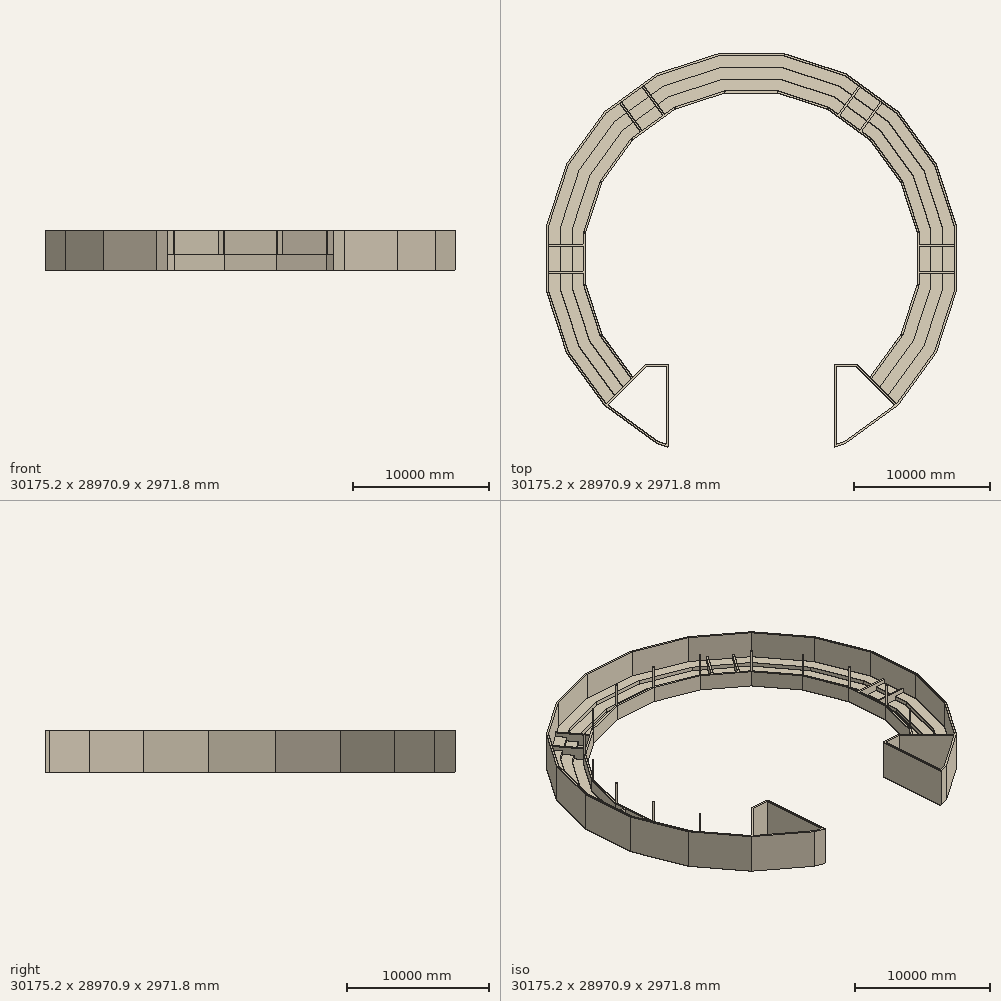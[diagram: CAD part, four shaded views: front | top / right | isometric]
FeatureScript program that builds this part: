
annotation { "Feature Type Name" : "Feature", "Feature Type Description" : "" }
export const myFeature = defineFeature(function(context is Context, id is Id, definition is map)
    precondition{}
    {
        {
            var Q0;
            Q0=qCreatedBy(makeId("Top.planeOp"),FACE);
            var sketch = newSketch(context, id + "F0", { "sketchPlane" : qUnion([Q0])});
            skLineSegment(sketch, "E0.0", {"start": v(-2389.64, 15087.6) * mm, "end": v(2389.64, 15087.6) * mm});
            skLineSegment(sketch, "E0.1", {"start": v(2389.64, 15087.6) * mm, "end": v(6935, 13610.72) * mm});
            skLineSegment(sketch, "E0.2", {"start": v(6935, 13610.72) * mm, "end": v(10801.53, 10801.53) * mm});
            skLineSegment(sketch, "E0.3", {"start": v(10801.53, 10801.53) * mm, "end": v(13610.72, 6935) * mm});
            skLineSegment(sketch, "E0.4", {"start": v(13610.72, 6935) * mm, "end": v(15087.6, 2389.64) * mm});
            skLineSegment(sketch, "E0.5", {"start": v(15087.6, 2389.64) * mm, "end": v(15087.6, -2389.64) * mm});
            skLineSegment(sketch, "E0.6", {"start": v(15087.6, -2389.64) * mm, "end": v(13610.72, -6935) * mm});
            skLineSegment(sketch, "E0.7", {"start": v(13610.72, -6935) * mm, "end": v(10801.53, -10801.53) * mm});
            skLineSegment(sketch, "E0.8", {"start": v(10801.53, -10801.53) * mm, "end": v(6935, -13610.72) * mm});
            skLineSegment(sketch, "E0.9", {"start": v(6935, -13610.72) * mm, "end": v(6096, -13883.33) * mm});
            skLineSegment(sketch, "E0.11", {"start": v(-6096, -13883.33) * mm, "end": v(-6935, -13610.72) * mm});
            skLineSegment(sketch, "E0.12", {"start": v(-6935, -13610.72) * mm, "end": v(-10801.53, -10801.53) * mm});
            skLineSegment(sketch, "E0.13", {"start": v(-10801.53, -10801.53) * mm, "end": v(-13610.72, -6935) * mm});
            skLineSegment(sketch, "E0.14", {"start": v(-13610.72, -6935) * mm, "end": v(-15087.6, -2389.64) * mm});
            skLineSegment(sketch, "E0.15", {"start": v(-15087.6, -2389.64) * mm, "end": v(-15087.6, 2389.64) * mm});
            skLineSegment(sketch, "E0.16", {"start": v(-15087.6, 2389.64) * mm, "end": v(-13610.72, 6935) * mm});
            skLineSegment(sketch, "E0.17", {"start": v(-13610.72, 6935) * mm, "end": v(-10801.53, 10801.53) * mm});
            skLineSegment(sketch, "E0.18", {"start": v(-10801.53, 10801.53) * mm, "end": v(-6935, 13610.72) * mm});
            skLineSegment(sketch, "E0.19", {"start": v(-6935, 13610.72) * mm, "end": v(-2389.64, 15087.6) * mm});
            skLineSegment(sketch, "E1", {"start": v(-6096, -7772.4) * mm, "end": v(-6096, -13883.33) * mm});
            skLineSegment(sketch, "E2", {"start": v(6096, -7772.4) * mm, "end": v(6096, -13883.33) * mm});
            skLineSegment(sketch, "E3", {"start": v(-7772.4, -7772.4) * mm, "end": v(-6096, -7772.4) * mm});
            skLineSegment(sketch, "E4", {"start": v(6096, -7772.4) * mm, "end": v(6705.6, -7772.4) * mm});
            skLineSegment(sketch, "E5.0", {"start": v(-1931.02, 12192) * mm, "end": v(1931.02, 12192) * mm});
            skLineSegment(sketch, "E5.1", {"start": v(1931.02, 12192) * mm, "end": v(5604.05, 10998.56) * mm});
            skLineSegment(sketch, "E5.2", {"start": v(5604.05, 10998.56) * mm, "end": v(6426.51, 10401) * mm});
            skLineSegment(sketch, "E5.3", {"start": v(8728.5, 8728.5) * mm, "end": v(10998.56, 5604.05) * mm});
            skLineSegment(sketch, "E5.4", {"start": v(10998.56, 5604.05) * mm, "end": v(12192, 1931.02) * mm});
            skLineSegment(sketch, "E5.5", {"start": v(12192, 1931.02) * mm, "end": v(12192, 914.4) * mm});
            skLineSegment(sketch, "E5.6", {"start": v(12192, -1931.02) * mm, "end": v(10998.56, -5604.05) * mm});
            skLineSegment(sketch, "E5.13", {"start": v(-8728.5, -8728.5) * mm, "end": v(-10998.56, -5604.05) * mm});
            skLineSegment(sketch, "E5.14", {"start": v(-10998.56, -5604.05) * mm, "end": v(-12192, -1931.02) * mm});
            skLineSegment(sketch, "E5.15", {"start": v(-12192, -1931.02) * mm, "end": v(-12192, -914.4) * mm});
            skLineSegment(sketch, "E5.16", {"start": v(-12192, 1931.02) * mm, "end": v(-10998.56, 5604.05) * mm});
            skLineSegment(sketch, "E5.17", {"start": v(-10998.56, 5604.05) * mm, "end": v(-8728.5, 8728.5) * mm});
            skLineSegment(sketch, "E5.18", {"start": v(-8728.5, 8728.5) * mm, "end": v(-7953.14, 9291.85) * mm});
            skLineSegment(sketch, "E5.19", {"start": v(-5604.05, 10998.56) * mm, "end": v(-1931.02, 12192) * mm});
            skLineSegment(sketch, "E6", {"start": v(-15087.6, 0) * mm, "end": v(-15087.6, 914.4) * mm});
            skLineSegment(sketch, "E7", {"start": v(-14935.2, 914.4) * mm, "end": v(-12344.4, 914.4) * mm});
            skPoint(sketch, "E7.endSnap0", {"position": v(15087.6, 0) * mm});
            skLineSegment(sketch, "E8", {"start": v(15087.6, 914.4) * mm, "end": v(15087.6, -914.4) * mm});
            skLineSegment(sketch, "E9", {"start": v(14935.2, -914.4) * mm, "end": v(12344.4, -914.4) * mm});
            skLineSegment(sketch, "E10.trimOffspring", {"start": v(12344.4, 914.4) * mm, "end": v(14935.2, 914.4) * mm});
            skLineSegment(sketch, "E11.trimOffspring", {"start": v(-12344.4, -914.4) * mm, "end": v(-14935.2, -914.4) * mm});
            skLineSegment(sketch, "E12.trimOffspring", {"start": v(-12192, 914.4) * mm, "end": v(-12192, 1931.02) * mm});
            skLineSegment(sketch, "E13.trimOffspring", {"start": v(12192, -914.4) * mm, "end": v(12192, -1931.02) * mm});
            skLineSegment(sketch, "E14", {"start": v(-8042.71, 9415.14) * mm, "end": v(-9565.55, 11511.14) * mm});
            skLineSegment(sketch, "E15", {"start": v(-9655.13, 11634.44) * mm, "end": v(-8128.5, 12743.6) * mm});
            skLineSegment(sketch, "E16", {"start": v(-8038.93, 12620.3) * mm, "end": v(-6516.1, 10524.3) * mm});
            skLineSegment(sketch, "E17.trimOffspring", {"start": v(-6426.51, 10401) * mm, "end": v(-5604.05, 10998.56) * mm});
            skLineSegment(sketch, "E18.MirrorCS", {"start": v(8038.93, 12620.3) * mm, "end": v(6516.1, 10524.3) * mm});
            skLineSegment(sketch, "E19.MirrorCS", {"start": v(7995.62, 9449.36) * mm, "end": v(9518.46, 11545.36) * mm});
            skLineSegment(sketch, "E20.trimOffspring", {"start": v(7906.04, 9326.06) * mm, "end": v(8728.5, 8728.5) * mm});
            skLineSegment(sketch, "E21.0", {"start": v(-2365.5, 14935.2) * mm, "end": v(2365.5, 14935.2) * mm});
            skLineSegment(sketch, "E21.1", {"start": v(2365.5, 14935.2) * mm, "end": v(6864.96, 13473.24) * mm});
            skLineSegment(sketch, "E21.2", {"start": v(6864.96, 13473.24) * mm, "end": v(7915.63, 12709.88) * mm});
            skLineSegment(sketch, "E21.3", {"start": v(10692.42, 10692.42) * mm, "end": v(13473.24, 6864.96) * mm});
            skLineSegment(sketch, "E21.4", {"start": v(13473.24, 6864.96) * mm, "end": v(14935.2, 2365.5) * mm});
            skLineSegment(sketch, "E21.5", {"start": v(14935.2, 2365.5) * mm, "end": v(14935.2, 1066.8) * mm});
            skLineSegment(sketch, "E21.6", {"start": v(14935.2, -2365.5) * mm, "end": v(13473.24, -6864.96) * mm});
            skLineSegment(sketch, "E21.12", {"start": v(-6864.96, -13473.24) * mm, "end": v(-10692.42, -10692.42) * mm});
            skLineSegment(sketch, "E21.13", {"start": v(-10692.42, -10692.42) * mm, "end": v(-13473.24, -6864.96) * mm});
            skLineSegment(sketch, "E21.14", {"start": v(-13473.24, -6864.96) * mm, "end": v(-14935.2, -2365.5) * mm});
            skLineSegment(sketch, "E21.15", {"start": v(-14935.2, -2365.5) * mm, "end": v(-14935.2, -1066.8) * mm});
            skLineSegment(sketch, "E21.16", {"start": v(-14935.2, 2365.5) * mm, "end": v(-13473.24, 6864.96) * mm});
            skLineSegment(sketch, "E21.17", {"start": v(-13473.24, 6864.96) * mm, "end": v(-10692.42, 10692.42) * mm});
            skLineSegment(sketch, "E21.18", {"start": v(-10692.42, 10692.42) * mm, "end": v(-9688.84, 11421.57) * mm});
            skLineSegment(sketch, "E21.19", {"start": v(-6864.96, 13473.24) * mm, "end": v(-2365.5, 14935.2) * mm});
            skLineSegment(sketch, "E22.trimOffspring", {"start": v(-7915.63, 12709.88) * mm, "end": v(-6864.96, 13473.24) * mm});
            skLineSegment(sketch, "E23", {"start": v(0, 12192) * mm, "end": v(0, 12344.4) * mm});
            skLineSegment(sketch, "E24.0", {"start": v(-1955.16, 12344.4) * mm, "end": v(1955.16, 12344.4) * mm});
            skLineSegment(sketch, "E24.1", {"start": v(1955.16, 12344.4) * mm, "end": v(5674.1, 11136.04) * mm});
            skLineSegment(sketch, "E24.2", {"start": v(5674.1, 11136.04) * mm, "end": v(6392.8, 10613.88) * mm});
            skLineSegment(sketch, "E24.3", {"start": v(8837.61, 8837.61) * mm, "end": v(11136.04, 5674.1) * mm});
            skLineSegment(sketch, "E24.4", {"start": v(11136.04, 5674.1) * mm, "end": v(12344.4, 1955.16) * mm});
            skLineSegment(sketch, "E24.5", {"start": v(12344.4, 1955.16) * mm, "end": v(12344.4, 1066.8) * mm});
            skLineSegment(sketch, "E24.6", {"start": v(12344.4, -1955.16) * mm, "end": v(11136.04, -5674.1) * mm});
            skLineSegment(sketch, "E24.13", {"start": v(-8837.61, -8837.61) * mm, "end": v(-11136.04, -5674.1) * mm});
            skLineSegment(sketch, "E24.14", {"start": v(-11136.04, -5674.1) * mm, "end": v(-12344.4, -1955.16) * mm});
            skLineSegment(sketch, "E24.15", {"start": v(-12344.4, -1955.16) * mm, "end": v(-12344.4, -1066.8) * mm});
            skLineSegment(sketch, "E24.16", {"start": v(-12344.4, 1955.16) * mm, "end": v(-11136.04, 5674.1) * mm});
            skLineSegment(sketch, "E24.17", {"start": v(-11136.04, 5674.1) * mm, "end": v(-8837.61, 8837.61) * mm});
            skLineSegment(sketch, "E24.18", {"start": v(-8837.61, 8837.61) * mm, "end": v(-8166, 9325.56) * mm});
            skLineSegment(sketch, "E24.19", {"start": v(-5674.1, 11136.04) * mm, "end": v(-1955.16, 12344.4) * mm});
            skPoint(sketch, "E24.0.midPoint", {"position": v(0, 12344.4) * mm});
            skLineSegment(sketch, "E25.trimOffspring", {"start": v(-6392.8, 10613.88) * mm, "end": v(-5674.1, 11136.04) * mm});
            skLineSegment(sketch, "E26.trimOffspring", {"start": v(8118.92, 9359.78) * mm, "end": v(8837.61, 8837.61) * mm});
            skLineSegment(sketch, "E27", {"start": v(-10692.42, -10692.42) * mm, "end": v(-7772.4, -7772.4) * mm});
            skLineSegment(sketch, "E28", {"start": v(-8837.61, -8837.61) * mm, "end": v(-10692.42, -10692.42) * mm});
            skLineSegment(sketch, "E29", {"start": v(-7709.27, -7924.8) * mm, "end": v(-10567.6, -10783.12) * mm});
            skLineSegment(sketch, "E30", {"start": v(-6096, -7772.4) * mm, "end": v(-6096, -7924.8) * mm});
            skLineSegment(sketch, "E31", {"start": v(-6248.4, -7924.8) * mm, "end": v(-7709.27, -7924.8) * mm});
            skPoint(sketch, "E32.orphan", {"position": v(-7556.87, -7772.4) * mm});
            skLineSegment(sketch, "E33", {"start": v(-6248.4, -7924.8) * mm, "end": v(-6248.4, -13673.57) * mm});
            skLineSegment(sketch, "E34.trimOffspring", {"start": v(-6248.4, -13673.57) * mm, "end": v(-6864.96, -13473.24) * mm});
            skLineSegment(sketch, "E35.MirrorCS", {"start": v(8728.5, -8728.5) * mm, "end": v(10998.56, -5604.05) * mm});
            skLineSegment(sketch, "E36.MirrorCS", {"start": v(7709.27, -7924.8) * mm, "end": v(10567.6, -10783.12) * mm});
            skLineSegment(sketch, "E37.MirrorCS", {"start": v(6248.4, -7924.8) * mm, "end": v(7709.27, -7924.8) * mm});
            skLineSegment(sketch, "E38.MirrorCS", {"start": v(7772.4, -7772.4) * mm, "end": v(6096, -7772.4) * mm});
            skPoint(sketch, "E39.MirrorP", {"position": v(7556.87, -7772.4) * mm});
            skLineSegment(sketch, "E40.MirrorCS", {"start": v(8837.61, -8837.61) * mm, "end": v(11136.04, -5674.1) * mm});
            skLineSegment(sketch, "E41.MirrorCS", {"start": v(10692.42, -10692.42) * mm, "end": v(7772.4, -7772.4) * mm});
            skLineSegment(sketch, "E42.MirrorCS", {"start": v(8837.61, -8837.61) * mm, "end": v(10692.42, -10692.42) * mm});
            skLineSegment(sketch, "E43.MirrorCS", {"start": v(6864.96, -13473.24) * mm, "end": v(10692.42, -10692.42) * mm});
            skLineSegment(sketch, "E44.MirrorCS", {"start": v(10692.42, -10692.42) * mm, "end": v(13473.24, -6864.96) * mm});
            skLineSegment(sketch, "E45.MirrorCS", {"start": v(6248.4, -13673.57) * mm, "end": v(6864.96, -13473.24) * mm});
            skLineSegment(sketch, "E46.MirrorCS", {"start": v(6248.4, -7924.8) * mm, "end": v(6248.4, -13673.57) * mm});
            skLineSegment(sketch, "E47.trimOffspring", {"start": v(-12344.4, 1066.8) * mm, "end": v(-12344.4, 1955.16) * mm});
            skLineSegment(sketch, "E48.trimOffspring", {"start": v(-14935.2, 1066.8) * mm, "end": v(-14935.2, 2365.5) * mm});
            skLineSegment(sketch, "E49", {"start": v(-14935.2, -1066.8) * mm, "end": v(-12344.4, -1066.8) * mm});
            skLineSegment(sketch, "E50.0", {"start": v(-14071.6, -2228.72) * mm, "end": v(-14071.6, -1066.8) * mm});
            skLineSegment(sketch, "E50.1", {"start": v(-14071.6, 2228.72) * mm, "end": v(-12694.17, 6468) * mm});
            skLineSegment(sketch, "E50.2", {"start": v(-12694.17, 6468) * mm, "end": v(-10074.15, 10074.15) * mm});
            skLineSegment(sketch, "E50.3", {"start": v(-10074.15, 10074.15) * mm, "end": v(-9181.23, 10722.9) * mm});
            skLineSegment(sketch, "E50.4", {"start": v(-6468, 12694.17) * mm, "end": v(-2228.72, 14071.6) * mm});
            skLineSegment(sketch, "E50.5", {"start": v(-2228.72, 14071.6) * mm, "end": v(2228.72, 14071.6) * mm});
            skLineSegment(sketch, "E50.6", {"start": v(2228.72, 14071.6) * mm, "end": v(6468, 12694.17) * mm});
            skLineSegment(sketch, "E50.7", {"start": v(6468, 12694.17) * mm, "end": v(7408.02, 12011.21) * mm});
            skLineSegment(sketch, "E50.8", {"start": v(10074.15, 10074.15) * mm, "end": v(12694.17, 6468) * mm});
            skLineSegment(sketch, "E50.9", {"start": v(12694.17, 6468) * mm, "end": v(14071.6, 2228.72) * mm});
            skLineSegment(sketch, "E50.10", {"start": v(14071.6, 2228.72) * mm, "end": v(14071.6, 1066.8) * mm});
            skLineSegment(sketch, "E50.11", {"start": v(14071.6, -2228.72) * mm, "end": v(12694.17, -6468) * mm});
            skLineSegment(sketch, "E50.12", {"start": v(12694.17, -6468) * mm, "end": v(10074.15, -10074.15) * mm});
            skLineSegment(sketch, "E50.18", {"start": v(-10074.15, -10074.15) * mm, "end": v(-12694.17, -6468) * mm});
            skLineSegment(sketch, "E50.19", {"start": v(-12694.17, -6468) * mm, "end": v(-14071.6, -2228.72) * mm});
            skLineSegment(sketch, "E51.0", {"start": v(-13208, -2091.94) * mm, "end": v(-13208, -1066.8) * mm});
            skLineSegment(sketch, "E51.1", {"start": v(-13208, 2091.94) * mm, "end": v(-11915.1, 6071.05) * mm});
            skLineSegment(sketch, "E51.2", {"start": v(-11915.1, 6071.05) * mm, "end": v(-9455.88, 9455.88) * mm});
            skLineSegment(sketch, "E51.3", {"start": v(-9455.88, 9455.88) * mm, "end": v(-8673.62, 10024.23) * mm});
            skLineSegment(sketch, "E51.4", {"start": v(-6071.05, 11915.1) * mm, "end": v(-2091.94, 13208) * mm});
            skLineSegment(sketch, "E51.5", {"start": v(-2091.94, 13208) * mm, "end": v(2091.94, 13208) * mm});
            skLineSegment(sketch, "E51.6", {"start": v(2091.94, 13208) * mm, "end": v(6071.05, 11915.1) * mm});
            skLineSegment(sketch, "E51.8", {"start": v(9455.88, 9455.88) * mm, "end": v(11915.1, 6071.05) * mm});
            skLineSegment(sketch, "E51.9", {"start": v(11915.1, 6071.05) * mm, "end": v(13208, 2091.94) * mm});
            skLineSegment(sketch, "E51.10", {"start": v(13208, 2091.94) * mm, "end": v(13208, 1066.8) * mm});
            skLineSegment(sketch, "E51.11", {"start": v(13208, -2091.94) * mm, "end": v(11915.1, -6071.05) * mm});
            skLineSegment(sketch, "E51.12", {"start": v(11915.1, -6071.05) * mm, "end": v(9455.88, -9455.88) * mm});
            skLineSegment(sketch, "E51.18", {"start": v(-9455.88, -9455.88) * mm, "end": v(-11915.1, -6071.05) * mm});
            skLineSegment(sketch, "E51.19", {"start": v(-11915.1, -6071.05) * mm, "end": v(-13208, -2091.94) * mm});
            skLineSegment(sketch, "E52.trimOffspring", {"start": v(-14071.6, 1066.8) * mm, "end": v(-14071.6, 2228.72) * mm});
            skLineSegment(sketch, "E53", {"start": v(-13208, 2091.94) * mm, "end": v(-13208, 1066.8) * mm});
            skLineSegment(sketch, "E54", {"start": v(-14935.2, 1066.8) * mm, "end": v(-12344.4, 1066.8) * mm});
            skLineSegment(sketch, "E55", {"start": v(-9688.84, 11421.57) * mm, "end": v(-8166, 9325.56) * mm});
            skLineSegment(sketch, "E56", {"start": v(-7915.63, 12709.88) * mm, "end": v(-6392.8, 10613.88) * mm});
            skLineSegment(sketch, "E57.trimOffspring", {"start": v(-7408.02, 12011.21) * mm, "end": v(-6468, 12694.17) * mm});
            skLineSegment(sketch, "E58.trimOffspring", {"start": v(-6900.4, 11312.55) * mm, "end": v(-6071.05, 11915.1) * mm});
            skLineSegment(sketch, "E59", {"start": v(6392.8, 10613.88) * mm, "end": v(7915.63, 12709.88) * mm});
            skLineSegment(sketch, "E60.trimOffspring", {"start": v(9134.14, 10757.11) * mm, "end": v(10074.15, 10074.15) * mm});
            skLineSegment(sketch, "E61.trimOffspring", {"start": v(8626.53, 10058.45) * mm, "end": v(9455.88, 9455.88) * mm});
            skLineSegment(sketch, "E62.trimOffspring", {"start": v(9641.75, 11455.78) * mm, "end": v(10692.42, 10692.42) * mm});
            skLineSegment(sketch, "E63", {"start": v(8118.92, 9359.78) * mm, "end": v(9641.75, 11455.78) * mm});
            skLineSegment(sketch, "E64", {"start": v(6071.05, 11915.1) * mm, "end": v(6900.4, 11312.55) * mm});
            skLineSegment(sketch, "E65.trimOffspring", {"start": v(12344.4, -1066.8) * mm, "end": v(12344.4, -1955.16) * mm});
            skLineSegment(sketch, "E66.trimOffspring", {"start": v(13208, -1066.8) * mm, "end": v(13208, -2091.94) * mm});
            skLineSegment(sketch, "E67.trimOffspring", {"start": v(14071.6, -1066.8) * mm, "end": v(14071.6, -2228.72) * mm});
            skLineSegment(sketch, "E68", {"start": v(12344.4, 1066.8) * mm, "end": v(14935.2, 1066.8) * mm});
            skLineSegment(sketch, "E69", {"start": v(12344.4, -1066.8) * mm, "end": v(14935.2, -1066.8) * mm});
            skLineSegment(sketch, "E70.trimOffspring", {"start": v(14935.2, -1066.8) * mm, "end": v(14935.2, -2365.5) * mm});
            skLineSegment(sketch, "E71", {"start": v(-8038.93, 12620.3) * mm, "end": v(-9565.55, 11511.14) * mm});
            skLineSegment(sketch, "E72", {"start": v(8038.93, 12620.3) * mm, "end": v(9518.46, 11545.36) * mm});
            skLineSegment(sketch, "E73", {"start": v(14935.2, -914.4) * mm, "end": v(14935.2, 914.4) * mm});
            skLineSegment(sketch, "E74", {"start": v(-14935.2, 914.4) * mm, "end": v(-14935.2, -914.4) * mm});
            skLineSegment(sketch, "E75", {"start": v(-14935.2, -914.4) * mm, "end": v(-14935.2, -1066.8) * mm});
            skLineSegment(sketch, "E76", {"start": v(-14935.2, 1066.8) * mm, "end": v(-14935.2, 914.4) * mm});
            skLineSegment(sketch, "E77", {"start": v(-9565.55, 11511.14) * mm, "end": v(-9688.84, 11421.57) * mm});
            skLineSegment(sketch, "E78", {"start": v(-7915.63, 12709.88) * mm, "end": v(-8038.93, 12620.3) * mm});
            skLineSegment(sketch, "E79", {"start": v(7915.63, 12709.88) * mm, "end": v(8038.93, 12620.3) * mm});
            skLineSegment(sketch, "E80", {"start": v(9518.46, 11545.36) * mm, "end": v(9641.75, 11455.78) * mm});
            skLineSegment(sketch, "E81", {"start": v(14935.2, 1066.8) * mm, "end": v(14935.2, 914.4) * mm});
            skLineSegment(sketch, "E82", {"start": v(14935.2, -914.4) * mm, "end": v(14935.2, -1066.8) * mm});
            skCircle(sketch, "E83", {"center": v(-11067.3, -5639.07) * mm, "radius": 60.96 * mm});
            skCircle(sketch, "E84.7.0", {"center": v(11067.3, -5639.07) * mm, "radius": 60.96 * mm});
            skCircle(sketch, "E84.8.0", {"center": v(12268.2, -1943.1) * mm, "radius": 60.96 * mm});
            skCircle(sketch, "E84.9.0", {"center": v(12268.2, 1943.1) * mm, "radius": 60.96 * mm});
            skCircle(sketch, "E84.10.0", {"center": v(11067.3, 5639.07) * mm, "radius": 60.96 * mm});
            skCircle(sketch, "E84.11.0", {"center": v(8783.06, 8783.06) * mm, "radius": 60.96 * mm});
            skCircle(sketch, "E84.12.0", {"center": v(5639.07, 11067.3) * mm, "radius": 60.96 * mm});
            skCircle(sketch, "E84.13.0", {"center": v(1943.1, 12268.2) * mm, "radius": 60.96 * mm});
            skCircle(sketch, "E84.14.0", {"center": v(-1943.1, 12268.2) * mm, "radius": 60.96 * mm});
            skCircle(sketch, "E84.15.0", {"center": v(-5639.07, 11067.3) * mm, "radius": 60.96 * mm});
            skCircle(sketch, "E84.16.0", {"center": v(-8783.06, 8783.06) * mm, "radius": 60.96 * mm});
            skCircle(sketch, "E84.17.0", {"center": v(-11067.3, 5639.07) * mm, "radius": 60.96 * mm});
            skCircle(sketch, "E84.18.0", {"center": v(-12268.2, 1943.1) * mm, "radius": 60.96 * mm});
            skCircle(sketch, "E84.19.0", {"center": v(-12268.2, -1943.1) * mm, "radius": 60.96 * mm});
            skLineSegment(sketch, "E85", {"start": v(-9057.94, 10812.48) * mm, "end": v(-7531.31, 11921.63) * mm});
            skLineSegment(sketch, "E86", {"start": v(-8550.33, 10113.81) * mm, "end": v(-7023.7, 11222.97) * mm});
            skLineSegment(sketch, "E87", {"start": v(-7953.14, 9291.85) * mm, "end": v(-6426.51, 10401) * mm});
            skLineSegment(sketch, "E88", {"start": v(-6516.1, 10524.3) * mm, "end": v(-8042.71, 9415.14) * mm});
            skLineSegment(sketch, "E89", {"start": v(-14071.6, 914.4) * mm, "end": v(-14071.6, -914.4) * mm});
            skLineSegment(sketch, "E90", {"start": v(-13208, 914.4) * mm, "end": v(-13208, -914.4) * mm});
            skLineSegment(sketch, "E91", {"start": v(-12344.4, 914.4) * mm, "end": v(-12344.4, -914.4) * mm});
            skLineSegment(sketch, "E92", {"start": v(-12192, 914.4) * mm, "end": v(-12192, -914.4) * mm});
            skLineSegment(sketch, "E93", {"start": v(6426.51, 10401) * mm, "end": v(7906.04, 9326.06) * mm});
            skLineSegment(sketch, "E94", {"start": v(6516.1, 10524.3) * mm, "end": v(7995.62, 9449.36) * mm});
            skLineSegment(sketch, "E95", {"start": v(7023.7, 11222.97) * mm, "end": v(8503.23, 10148.03) * mm});
            skLineSegment(sketch, "E96", {"start": v(7531.31, 11921.63) * mm, "end": v(9010.84, 10846.7) * mm});
            skLineSegment(sketch, "E97", {"start": v(12192, 914.4) * mm, "end": v(12192, -914.4) * mm});
            skLineSegment(sketch, "E98", {"start": v(12344.4, 914.4) * mm, "end": v(12344.4, -914.4) * mm});
            skLineSegment(sketch, "E99", {"start": v(14071.6, 914.4) * mm, "end": v(14071.6, -914.4) * mm});
            skLineSegment(sketch, "E100", {"start": v(13208, 914.4) * mm, "end": v(13208, -914.4) * mm});
            skSolve(sketch);
        }
        {
            var Q0;
            Q0=makeQuery(id+"F0.imprint","IMPRINT",FACE,{"disambiguationData":[TD([[makeQuery(id+"F0.imprint","IMPRINT",EDGE,{"derivedFrom":sQuery(id+"F0.wireOp",EDGE,"E0.0")}),-1.0]])]});
            extrude(context, id + "F1", {"entities" : qUnion([Q0]), "depth" : 2971.8 * mm, "offsetDistance" : 30.48 * mm});
        }
        {
            var Q0;
            {var subQ2=sQuery(id+"F0.wireOp",EDGE,"E24.13");Q0=makeQuery(id+"F0.imprint","IMPRINT",FACE,{"disambiguationData":[TD([[makeQuery(id+"F0.imprint","IMPRINT",EDGE,{"derivedFrom":subQ2}),1.0]])]});}
            var Q1;
            Q1=makeQuery(id+"F0.imprint","IMPRINT",FACE,{"disambiguationData":[TD([[makeQuery(id+"F0.imprint","IMPRINT",EDGE,{"derivedFrom":sQuery(id+"F0.wireOp",EDGE,"E24.16")}),1.0]])]});
            var Q2;
            Q2=makeQuery(id+"F0.imprint","IMPRINT",FACE,{"disambiguationData":[TD([[makeQuery(id+"F0.imprint","IMPRINT",EDGE,{"derivedFrom":sQuery(id+"F0.wireOp",EDGE,"E24.6")}),1.0]])]});
            var Q3;
            Q3=makeQuery(id+"F0.imprint","IMPRINT",FACE,{"disambiguationData":[TD([[makeQuery(id+"F0.imprint","IMPRINT",EDGE,{"derivedFrom":sQuery(id+"F0.wireOp",EDGE,"E24.3")}),1.0]])]});
            var Q4;
            {var subQ9=sQuery(id+"F0.wireOp",EDGE,"E24.1");Q4=makeQuery(id+"F0.imprint","IMPRINT",FACE,{"disambiguationData":[TD([[makeQuery(id+"F0.imprint","IMPRINT",EDGE,{"derivedFrom":subQ9}),1.0]])]});}
            var Q5;
            {var subQ2=sQuery(id+"F0.wireOp",EDGE,"E90");Q5=makeQuery(id+"F0.imprint","IMPRINT",FACE,{"disambiguationData":[TD([[makeQuery(id+"F0.imprint","IMPRINT",EDGE,{"derivedFrom":subQ2}),1.0]])]});}
            var Q6;
            {var subQ2=sQuery(id+"F0.wireOp",EDGE,"E86");Q6=makeQuery(id+"F0.imprint","IMPRINT",FACE,{"disambiguationData":[TD([[makeQuery(id+"F0.imprint","IMPRINT",EDGE,{"derivedFrom":subQ2}),-1.0]])]});}
            var Q7;
            {var subQ0=sQuery(id+"F0.wireOp",EDGE,"E94");Q7=makeQuery(id+"F0.imprint","IMPRINT",FACE,{"disambiguationData":[TD([[makeQuery(id+"F0.imprint","IMPRINT",EDGE,{"derivedFrom":subQ0}),1.0]])]});}
            var Q8;
            {var subQ0=sQuery(id+"F0.wireOp",EDGE,"E98");Q8=makeQuery(id+"F0.imprint","IMPRINT",FACE,{"disambiguationData":[TD([[makeQuery(id+"F0.imprint","IMPRINT",EDGE,{"derivedFrom":subQ0}),1.0]])]});}
            extrude(context, id + "F2", {"entities" : qUnion([Q0, Q1, Q2, Q3, Q4, Q5, Q6, Q7, Q8]), "depth" : 304.8 * mm, "offsetDistance" : 30.48 * mm});
        }
        {
            var Q0;
            Q0=makeQuery(id+"F0.imprint","IMPRINT",FACE,{"disambiguationData":[TD([[makeQuery(id+"F0.imprint","IMPRINT",EDGE,{"derivedFrom":sQuery(id+"F0.wireOp",EDGE,"E50.1")}),-1.0]])]});
            var Q1;
            {var subQ0=sQuery(id+"F0.wireOp",EDGE,"E50.0");Q1=makeQuery(id+"F0.imprint","IMPRINT",FACE,{"disambiguationData":[TD([[makeQuery(id+"F0.imprint","IMPRINT",EDGE,{"derivedFrom":subQ0}),-1.0]])]});}
            var Q2;
            Q2=makeQuery(id+"F0.imprint","IMPRINT",FACE,{"disambiguationData":[TD([[makeQuery(id+"F0.imprint","IMPRINT",EDGE,{"derivedFrom":sQuery(id+"F0.wireOp",EDGE,"E50.4")}),-1.0]])]});
            var Q3;
            Q3=makeQuery(id+"F0.imprint","IMPRINT",FACE,{"disambiguationData":[TD([[makeQuery(id+"F0.imprint","IMPRINT",EDGE,{"derivedFrom":sQuery(id+"F0.wireOp",EDGE,"E50.8")}),-1.0]])]});
            var Q4;
            Q4=makeQuery(id+"F0.imprint","IMPRINT",FACE,{"disambiguationData":[TD([[makeQuery(id+"F0.imprint","IMPRINT",EDGE,{"derivedFrom":sQuery(id+"F0.wireOp",EDGE,"E50.11")}),-1.0]])]});
            var Q5;
            {var subQ0=sQuery(id+"F0.wireOp",EDGE,"E89");Q5=makeQuery(id+"F0.imprint","IMPRINT",FACE,{"disambiguationData":[TD([[makeQuery(id+"F0.imprint","IMPRINT",EDGE,{"derivedFrom":subQ0}),1.0]])]});}
            var Q6;
            {var subQ0=sQuery(id+"F0.wireOp",EDGE,"E85");Q6=makeQuery(id+"F0.imprint","IMPRINT",FACE,{"disambiguationData":[TD([[makeQuery(id+"F0.imprint","IMPRINT",EDGE,{"derivedFrom":subQ0}),-1.0]])]});}
            var Q7;
            {var subQ0=sQuery(id+"F0.wireOp",EDGE,"E95");Q7=makeQuery(id+"F0.imprint","IMPRINT",FACE,{"disambiguationData":[TD([[makeQuery(id+"F0.imprint","IMPRINT",EDGE,{"derivedFrom":subQ0}),1.0]])]});}
            var Q8;
            {var subQ0=sQuery(id+"F0.wireOp",EDGE,"E99");Q8=makeQuery(id+"F0.imprint","IMPRINT",FACE,{"disambiguationData":[TD([[makeQuery(id+"F0.imprint","IMPRINT",EDGE,{"derivedFrom":subQ0}),-1.0]])]});}
            extrude(context, id + "F3", {"entities" : qUnion([Q0, Q1, Q2, Q3, Q4, Q5, Q6, Q7, Q8]), "operationType" : NewBodyOperationType.ADD, "depth" : 609.6 * mm, "offsetDistance" : 30.48 * mm});
        }
        {
            var Q0;
            {var subQ3=sQuery(id+"F0.wireOp",EDGE,"E21.13");Q0=makeQuery(id+"F0.imprint","IMPRINT",FACE,{"disambiguationData":[TD([[makeQuery(id+"F0.imprint","IMPRINT",EDGE,{"derivedFrom":subQ3}),-1.0]])]});}
            var Q1;
            Q1=makeQuery(id+"F0.imprint","IMPRINT",FACE,{"disambiguationData":[TD([[makeQuery(id+"F0.imprint","IMPRINT",EDGE,{"derivedFrom":sQuery(id+"F0.wireOp",EDGE,"E21.16")}),-1.0]])]});
            var Q2;
            Q2=makeQuery(id+"F0.imprint","IMPRINT",FACE,{"disambiguationData":[TD([[makeQuery(id+"F0.imprint","IMPRINT",EDGE,{"derivedFrom":sQuery(id+"F0.wireOp",EDGE,"E21.0")}),-1.0]])]});
            var Q3;
            Q3=makeQuery(id+"F0.imprint","IMPRINT",FACE,{"disambiguationData":[TD([[makeQuery(id+"F0.imprint","IMPRINT",EDGE,{"derivedFrom":sQuery(id+"F0.wireOp",EDGE,"E21.3")}),-1.0]])]});
            var Q4;
            Q4=makeQuery(id+"F0.imprint","IMPRINT",FACE,{"disambiguationData":[TD([[makeQuery(id+"F0.imprint","IMPRINT",EDGE,{"derivedFrom":sQuery(id+"F0.wireOp",EDGE,"E21.6")}),-1.0]])]});
            var Q5;
            {var subQ0=sQuery(id+"F0.wireOp",EDGE,"E74");Q5=makeQuery(id+"F0.imprint","IMPRINT",FACE,{"disambiguationData":[TD([[makeQuery(id+"F0.imprint","IMPRINT",EDGE,{"derivedFrom":subQ0}),1.0]])]});}
            var Q6;
            {var subQ0=sQuery(id+"F0.wireOp",EDGE,"E71");Q6=makeQuery(id+"F0.imprint","IMPRINT",FACE,{"disambiguationData":[TD([[makeQuery(id+"F0.imprint","IMPRINT",EDGE,{"derivedFrom":subQ0}),1.0]])]});}
            var Q7;
            {var subQ0=sQuery(id+"F0.wireOp",EDGE,"E72");Q7=makeQuery(id+"F0.imprint","IMPRINT",FACE,{"disambiguationData":[TD([[makeQuery(id+"F0.imprint","IMPRINT",EDGE,{"derivedFrom":subQ0}),-1.0]])]});}
            var Q8;
            {var subQ0=sQuery(id+"F0.wireOp",EDGE,"E73");Q8=makeQuery(id+"F0.imprint","IMPRINT",FACE,{"disambiguationData":[TD([[makeQuery(id+"F0.imprint","IMPRINT",EDGE,{"derivedFrom":subQ0}),1.0]])]});}
            extrude(context, id + "F4", {"entities" : qUnion([Q0, Q1, Q2, Q3, Q4, Q5, Q6, Q7, Q8]), "operationType" : NewBodyOperationType.ADD, "depth" : 914.4 * mm, "offsetDistance" : 30.48 * mm});
        }
        {
            var Q0;
            {var subQ7=sQuery(id+"F0.wireOp",EDGE,"E5.19");Q0=makeQuery(id+"F0.imprint","IMPRINT",FACE,{"disambiguationData":[TD([[makeQuery(id+"F0.imprint","IMPRINT",EDGE,{"derivedFrom":subQ7}),1.0]])]});}
            var Q1;
            Q1=makeQuery(id+"F0.imprint","IMPRINT",FACE,{"disambiguationData":[TD([[makeQuery(id+"F0.imprint","IMPRINT",EDGE,{"derivedFrom":sQuery(id+"F0.wireOp",EDGE,"E5.16")}),1.0]])]});
            var Q2;
            {var subQ7=sQuery(id+"F0.wireOp",EDGE,"E5.1");Q2=makeQuery(id+"F0.imprint","IMPRINT",FACE,{"disambiguationData":[TD([[makeQuery(id+"F0.imprint","IMPRINT",EDGE,{"derivedFrom":subQ7}),1.0]])]});}
            var Q3;
            Q3=makeQuery(id+"F0.imprint","IMPRINT",FACE,{"disambiguationData":[TD([[makeQuery(id+"F0.imprint","IMPRINT",EDGE,{"derivedFrom":sQuery(id+"F0.wireOp",EDGE,"E5.3")}),1.0]])]});
            var Q4;
            Q4=makeQuery(id+"F0.imprint","IMPRINT",FACE,{"disambiguationData":[TD([[makeQuery(id+"F0.imprint","IMPRINT",EDGE,{"derivedFrom":sQuery(id+"F0.wireOp",EDGE,"E5.6")}),1.0]])]});
            var Q5;
            {var subQ6=sQuery(id+"F0.wireOp",EDGE,"E5.13");Q5=makeQuery(id+"F0.imprint","IMPRINT",FACE,{"disambiguationData":[TD([[makeQuery(id+"F0.imprint","IMPRINT",EDGE,{"derivedFrom":subQ6}),1.0]])]});}
            extrude(context, id + "F5", {"entities" : qUnion([Q0, Q1, Q2, Q3, Q4, Q5]), "operationType" : NewBodyOperationType.ADD, "depth" : 1219.2 * mm, "offsetDistance" : 30.48 * mm});
        }
        {
            var Q0;
            Q0=makeQuery(id+"F0.imprint","IMPRINT",FACE,{"disambiguationData":[TD([[makeQuery(id+"F0.imprint","IMPRINT",EDGE,{"derivedFrom":sQuery(id+"F0.wireOp",EDGE,"E83")}),1.0]])]});
            var Q1;
            Q1=makeQuery(id+"F0.imprint","IMPRINT",FACE,{"disambiguationData":[TD([[makeQuery(id+"F0.imprint","IMPRINT",EDGE,{"derivedFrom":sQuery(id+"F0.wireOp",EDGE,"E84.19.0")}),1.0]])]});
            var Q2;
            Q2=makeQuery(id+"F0.imprint","IMPRINT",FACE,{"disambiguationData":[TD([[makeQuery(id+"F0.imprint","IMPRINT",EDGE,{"derivedFrom":sQuery(id+"F0.wireOp",EDGE,"E84.18.0")}),1.0]])]});
            var Q3;
            Q3=makeQuery(id+"F0.imprint","IMPRINT",FACE,{"disambiguationData":[TD([[makeQuery(id+"F0.imprint","IMPRINT",EDGE,{"derivedFrom":sQuery(id+"F0.wireOp",EDGE,"E84.17.0")}),1.0]])]});
            var Q4;
            Q4=makeQuery(id+"F0.imprint","IMPRINT",FACE,{"disambiguationData":[TD([[makeQuery(id+"F0.imprint","IMPRINT",EDGE,{"derivedFrom":sQuery(id+"F0.wireOp",EDGE,"E84.16.0")}),1.0]])]});
            var Q5;
            Q5=makeQuery(id+"F0.imprint","IMPRINT",FACE,{"disambiguationData":[TD([[makeQuery(id+"F0.imprint","IMPRINT",EDGE,{"derivedFrom":sQuery(id+"F0.wireOp",EDGE,"E84.15.0")}),1.0]])]});
            var Q6;
            Q6=makeQuery(id+"F0.imprint","IMPRINT",FACE,{"disambiguationData":[TD([[makeQuery(id+"F0.imprint","IMPRINT",EDGE,{"derivedFrom":sQuery(id+"F0.wireOp",EDGE,"E84.14.0")}),1.0]])]});
            var Q7;
            Q7=makeQuery(id+"F0.imprint","IMPRINT",FACE,{"disambiguationData":[TD([[makeQuery(id+"F0.imprint","IMPRINT",EDGE,{"derivedFrom":sQuery(id+"F0.wireOp",EDGE,"E84.13.0")}),1.0]])]});
            var Q8;
            Q8=makeQuery(id+"F0.imprint","IMPRINT",FACE,{"disambiguationData":[TD([[makeQuery(id+"F0.imprint","IMPRINT",EDGE,{"derivedFrom":sQuery(id+"F0.wireOp",EDGE,"E84.12.0")}),1.0]])]});
            var Q9;
            Q9=makeQuery(id+"F0.imprint","IMPRINT",FACE,{"disambiguationData":[TD([[makeQuery(id+"F0.imprint","IMPRINT",EDGE,{"derivedFrom":sQuery(id+"F0.wireOp",EDGE,"E84.11.0")}),1.0]])]});
            var Q10;
            Q10=makeQuery(id+"F0.imprint","IMPRINT",FACE,{"disambiguationData":[TD([[makeQuery(id+"F0.imprint","IMPRINT",EDGE,{"derivedFrom":sQuery(id+"F0.wireOp",EDGE,"E84.10.0")}),1.0]])]});
            var Q11;
            Q11=makeQuery(id+"F0.imprint","IMPRINT",FACE,{"disambiguationData":[TD([[makeQuery(id+"F0.imprint","IMPRINT",EDGE,{"derivedFrom":sQuery(id+"F0.wireOp",EDGE,"E84.9.0")}),1.0]])]});
            var Q12;
            Q12=makeQuery(id+"F0.imprint","IMPRINT",FACE,{"disambiguationData":[TD([[makeQuery(id+"F0.imprint","IMPRINT",EDGE,{"derivedFrom":sQuery(id+"F0.wireOp",EDGE,"E84.8.0")}),1.0]])]});
            var Q13;
            Q13=makeQuery(id+"F0.imprint","IMPRINT",FACE,{"disambiguationData":[TD([[makeQuery(id+"F0.imprint","IMPRINT",EDGE,{"derivedFrom":sQuery(id+"F0.wireOp",EDGE,"E84.7.0")}),1.0]])]});
            extrude(context, id + "F6", {"entities" : qUnion([Q0, Q1, Q2, Q3, Q4, Q5, Q6, Q7, Q8, Q9, Q10, Q11, Q12, Q13]), "operationType" : NewBodyOperationType.ADD, "depth" : 2971.8 * mm, "offsetDistance" : 30.48 * mm});
        }
    });
